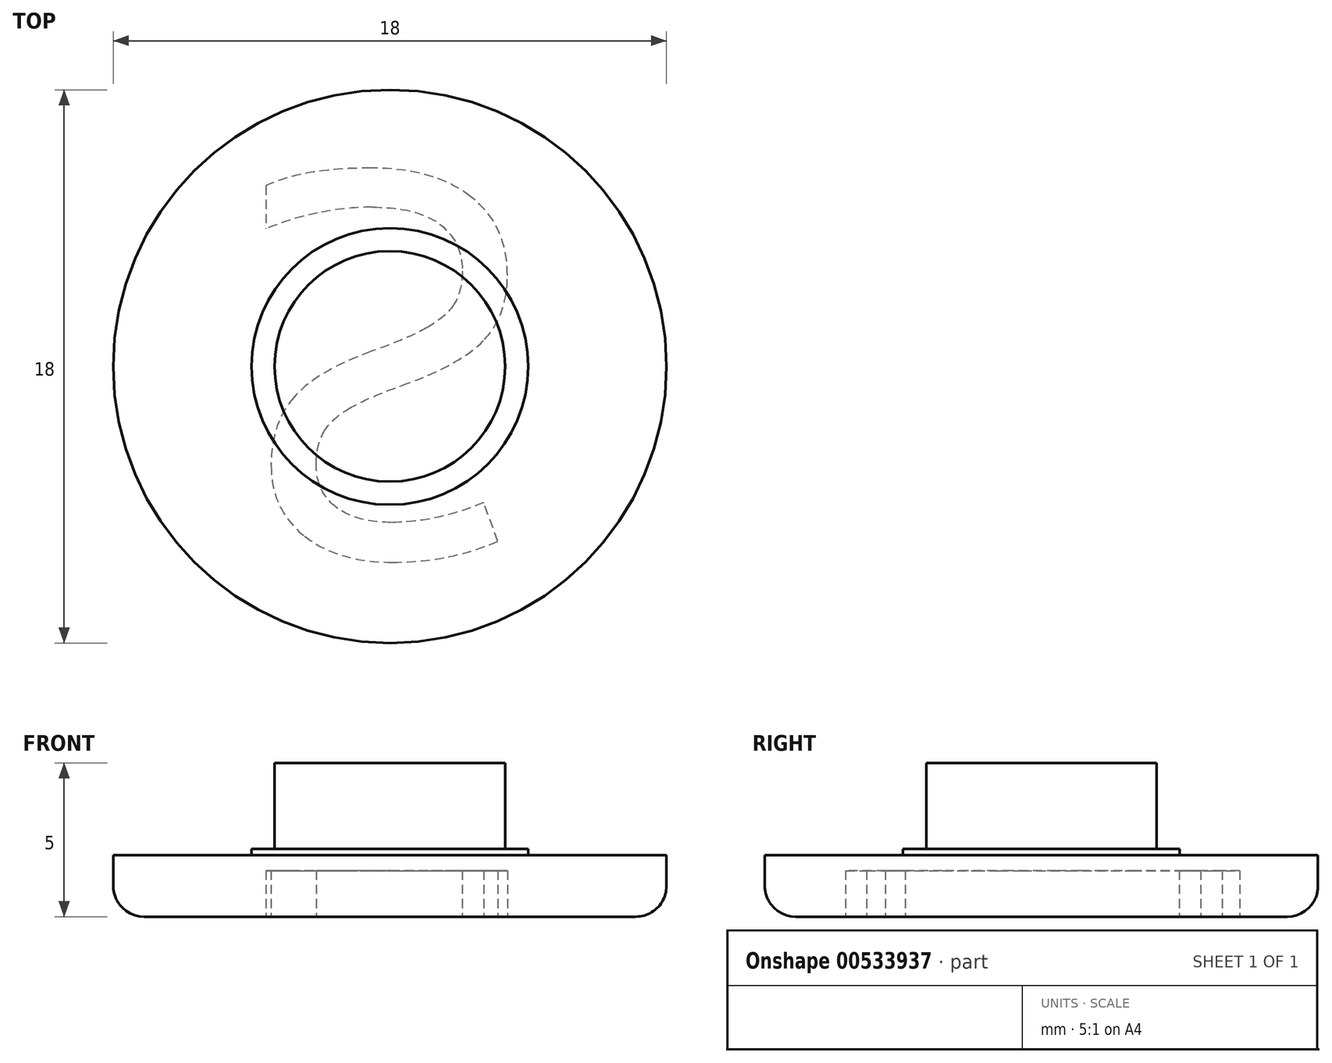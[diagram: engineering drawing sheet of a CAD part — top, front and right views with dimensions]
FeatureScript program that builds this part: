
annotation { "Feature Type Name" : "Feature", "Feature Type Description" : "" }
export const myFeature = defineFeature(function(context is Context, id is Id, definition is map)
    precondition{}
    {
        {
            var Q0;
            Q0=qCreatedBy(makeId("Top.planeOp"),FACE);
            var sketch = newSketch(context, id + "F0", { "sketchPlane" : qUnion([Q0])});
            skCircle(sketch, "E0", {"center": v(0, 0) * mm, "radius": 9 * mm});
            skSolve(sketch);
        }
        {
            var Q0;
            Q0=makeQuery(id+"F0.imprint","IMPRINT",FACE,{"disambiguationData":[TD([[makeQuery(id+"F0.imprint","IMPRINT",EDGE,{"derivedFrom":sQuery(id+"F0.wireOp",EDGE,"E0")}),1.0]])]});
            extrude(context, id + "F1", {"entities" : qUnion([Q0]), "depth" : 2 * mm});
        }
        {
            var Q0;
            Q0=makeQuery(id+"F1.opExtrude","CAP_FACE",FACE,{"disambiguationData":[OSD([sQuery(id+"F0.wireOp",EDGE,"E0")])],"isStart":false});
            var sketch = newSketch(context, id + "F2", { "sketchPlane" : qUnion([Q0])});
            skCircle(sketch, "E1", {"center": v(0, 0) * mm, "radius": 3.75 * mm});
            skSolve(sketch);
        }
        {
            var Q0;
            Q0=makeQuery(id+"F2.imprint","IMPRINT",FACE,{"disambiguationData":[TD([[makeQuery(id+"F2.imprint","IMPRINT",EDGE,{"derivedFrom":sQuery(id+"F2.wireOp",EDGE,"E1")}),1.0]])]});
            extrude(context, id + "F3", {"entities" : qUnion([Q0]), "operationType" : NewBodyOperationType.ADD, "depth" : 3 * mm});
        }
        {
            var Q0;
            Q0=makeQuery(id+"F1.opExtrude","CAP_EDGE",EDGE,{"disambiguationData":[OSD([sQuery(id+"F0.wireOp",EDGE,"E0")])],"isStart":true});
            fillet(context, id + "F4", {"entities" : qUnion([Q0]), "radius" : 1 * mm, "tangentPropagation" : true, "allowEdgeOverflow" : false});
        }
        {
            var Q0;
            Q0=makeQuery(id+"F1.opExtrude","CAP_FACE",FACE,{"disambiguationData":[OSD([sQuery(id+"F0.wireOp",EDGE,"E0")])],"isStart":true});
            var sketch = newSketch(context, id + "F5", { "sketchPlane" : qUnion([Q0])});
            skText(sketch, "E2", { "text": "S", "fontName": "OpenSans-Regular.ttf"});
            const initialGuessF5  = {"E2": [-0.00493, -0.00628, 1, 0, 0.01258]};
            skSetInitialGuess(sketch, initialGuessF5);
            skSolve(sketch);
        }
        {
            var Q0;
            Q0=qSketchRegion(id+"F5",true);
            extrude(context, id + "F6", {"entities" : qUnion([Q0]), "operationType" : NewBodyOperationType.REMOVE, "oppositeDirection" : true, "depth" : 1.5 * mm});
        }
        {
            var Q0;
            Q0=makeQuery(id+"F1.opExtrude","CAP_FACE",FACE,{"disambiguationData":[OSD([sQuery(id+"F0.wireOp",EDGE,"E0")])],"isStart":false});
            var sketch = newSketch(context, id + "F7", { "sketchPlane" : qUnion([Q0])});
            skCircle(sketch, "E3", {"center": v(0, 0) * mm, "radius": 4.5 * mm});
            skSolve(sketch);
        }
        {
            var Q0;
            Q0=makeQuery(id+"F7.imprint","IMPRINT",FACE,{"disambiguationData":[TD([[makeQuery(id+"F7.imprint","IMPRINT",EDGE,{"derivedFrom":sQuery(id+"F7.wireOp",EDGE,"E3")}),1.0]])]});
            extrude(context, id + "F8", {"entities" : qUnion([Q0]), "operationType" : NewBodyOperationType.ADD, "depth" : .2 * mm});
        }
    });
